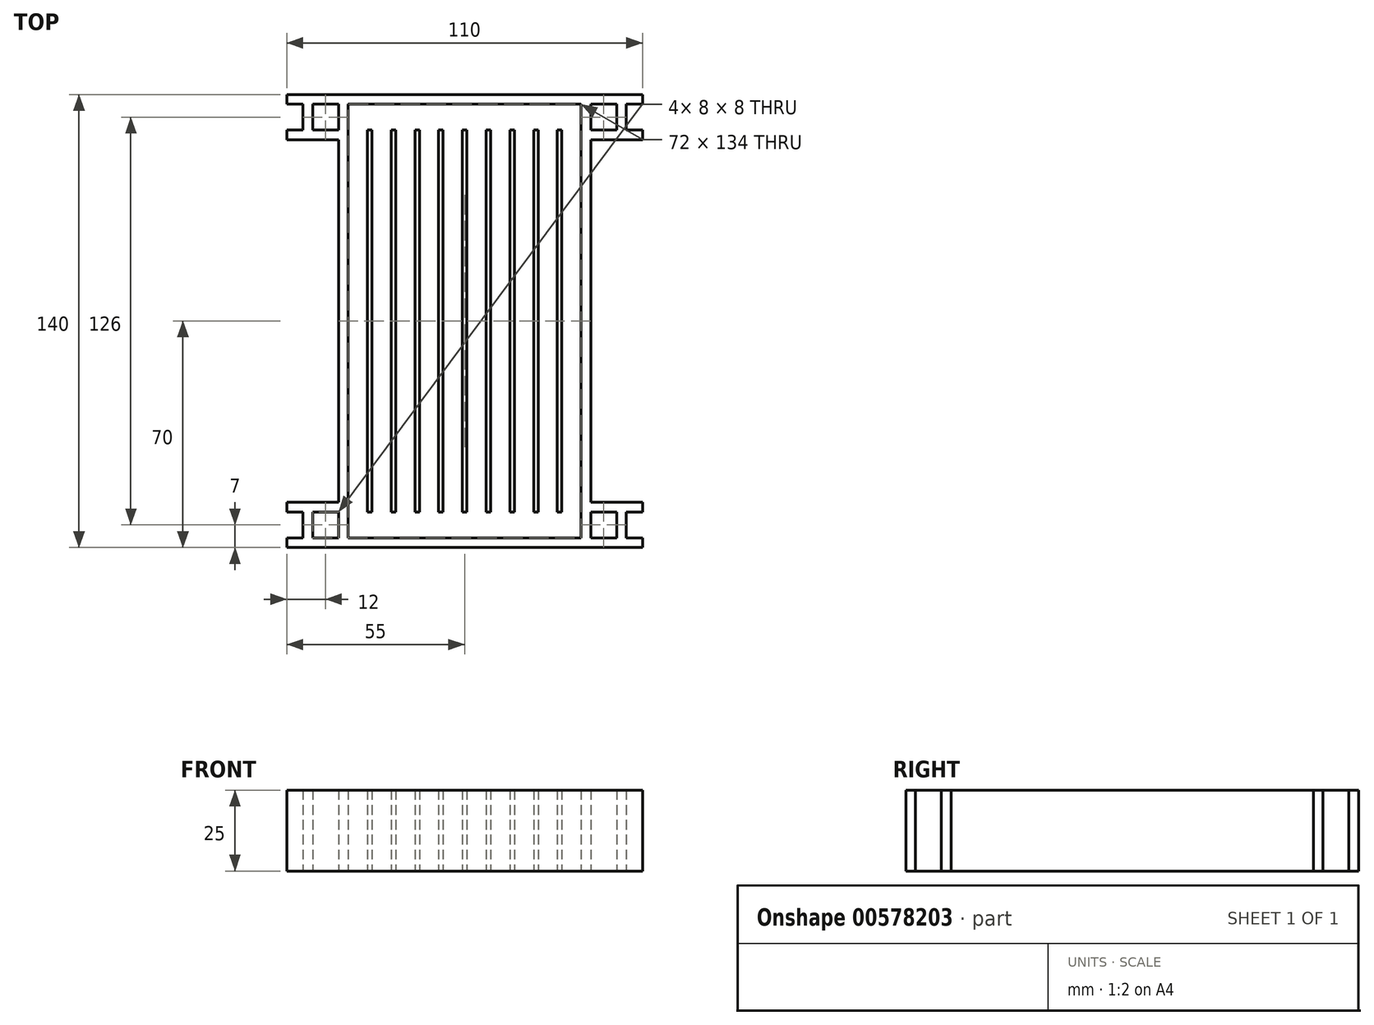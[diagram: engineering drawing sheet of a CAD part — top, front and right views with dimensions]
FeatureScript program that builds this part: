
annotation { "Feature Type Name" : "Feature", "Feature Type Description" : "" }
export const myFeature = defineFeature(function(context is Context, id is Id, definition is map)
    precondition{}
    {
        {
            var Q0;
            Q0=qCreatedBy(makeId("Top.planeOp"),FACE);
            var sketch = newSketch(context, id + "F0", { "sketchPlane" : qUnion([Q0])});
            skLineSegment(sketch, "E0.bottom", {"start": v(-55, 70) * mm, "end": v(55, 70) * mm});
            skLineSegment(sketch, "E0.top", {"start": v(-55, -70) * mm, "end": v(55, -70) * mm});
            skLineSegment(sketch, "E0.left", {"start": v(-55, 70) * mm, "end": v(-55, 67) * mm});
            skLineSegment(sketch, "E0.right", {"start": v(55, 70) * mm, "end": v(55, 67) * mm});
            skLineSegment(sketch, "E1", {"start": v(-55, 67) * mm, "end": v(-50, 67) * mm});
            skLineSegment(sketch, "E2", {"start": v(-50, 67) * mm, "end": v(-50, 59) * mm});
            skLineSegment(sketch, "E3", {"start": v(-39, 67) * mm, "end": v(-39, 59) * mm});
            skLineSegment(sketch, "E4", {"start": v(-50, 56) * mm, "end": v(-39, 56) * mm});
            skLineSegment(sketch, "E5", {"start": v(-47, 67) * mm, "end": v(-47, 59) * mm});
            skLineSegment(sketch, "E6", {"start": v(-47, 59) * mm, "end": v(-39, 59) * mm});
            skLineSegment(sketch, "E7", {"start": v(-36, 67) * mm, "end": v(-36, 0) * mm});
            skLineSegment(sketch, "E8.bottom", {"start": v(-30.06, 59) * mm, "end": v(-28.66, 59) * mm});
            skLineSegment(sketch, "E8.left", {"start": v(-30.06, 59) * mm, "end": v(-30.06, 0) * mm});
            skLineSegment(sketch, "E8.right", {"start": v(-28.66, 59) * mm, "end": v(-28.66, 0) * mm});
            skLineSegment(sketch, "E9.MirrorCS", {"start": v(39, 67) * mm, "end": v(39, 59) * mm});
            skLineSegment(sketch, "E10.MirrorCS", {"start": v(36, 67) * mm, "end": v(36, 0) * mm});
            skLineSegment(sketch, "E11.MirrorCS", {"start": v(47, 59) * mm, "end": v(39, 59) * mm});
            skLineSegment(sketch, "E12.MirrorCS", {"start": v(50, 56) * mm, "end": v(39, 56) * mm});
            skLineSegment(sketch, "E13.MirrorCS", {"start": v(50, 67) * mm, "end": v(50, 59) * mm});
            skLineSegment(sketch, "E14.MirrorCS", {"start": v(47, 67) * mm, "end": v(47, 59) * mm});
            skLineSegment(sketch, "E15.1.0.0", {"start": v(-21.32, 59) * mm, "end": v(-21.32, 0) * mm});
            skLineSegment(sketch, "E15.1.0.1", {"start": v(-22.72, 59) * mm, "end": v(-22.72, 0) * mm});
            skLineSegment(sketch, "E15.1.0.2", {"start": v(-22.72, 59) * mm, "end": v(-21.32, 59) * mm});
            skLineSegment(sketch, "E15.2.0.0", {"start": v(-13.98, 59) * mm, "end": v(-13.98, 0) * mm});
            skLineSegment(sketch, "E15.2.0.1", {"start": v(-15.38, 59) * mm, "end": v(-15.38, 0) * mm});
            skLineSegment(sketch, "E15.2.0.2", {"start": v(-15.38, 59) * mm, "end": v(-13.98, 59) * mm});
            skLineSegment(sketch, "E15.3.0.0", {"start": v(-6.64, 59) * mm, "end": v(-6.64, 0) * mm});
            skLineSegment(sketch, "E15.3.0.1", {"start": v(-8.04, 59) * mm, "end": v(-8.04, 0) * mm});
            skLineSegment(sketch, "E15.3.0.2", {"start": v(-8.04, 59) * mm, "end": v(-6.64, 59) * mm});
            skLineSegment(sketch, "E15.4.0.0", {"start": v(0.7, 59) * mm, "end": v(0.7, 0) * mm});
            skLineSegment(sketch, "E15.4.0.1", {"start": v(-0.7, 59) * mm, "end": v(-0.7, 0) * mm});
            skLineSegment(sketch, "E15.4.0.2", {"start": v(-0.7, 59) * mm, "end": v(0.7, 59) * mm});
            skLineSegment(sketch, "E15.5.0.0", {"start": v(8.04, 59) * mm, "end": v(8.04, 0) * mm});
            skLineSegment(sketch, "E15.5.0.1", {"start": v(6.64, 59) * mm, "end": v(6.64, 0) * mm});
            skLineSegment(sketch, "E15.5.0.2", {"start": v(6.64, 59) * mm, "end": v(8.04, 59) * mm});
            skLineSegment(sketch, "E15.6.0.0", {"start": v(15.38, 59) * mm, "end": v(15.38, 0) * mm});
            skLineSegment(sketch, "E15.6.0.1", {"start": v(13.98, 59) * mm, "end": v(13.98, 0) * mm});
            skLineSegment(sketch, "E15.6.0.2", {"start": v(13.98, 59) * mm, "end": v(15.38, 59) * mm});
            skLineSegment(sketch, "E15.7.0.0", {"start": v(22.72, 59) * mm, "end": v(22.72, 0) * mm});
            skLineSegment(sketch, "E15.7.0.1", {"start": v(21.32, 59) * mm, "end": v(21.32, 0) * mm});
            skLineSegment(sketch, "E15.7.0.2", {"start": v(21.32, 59) * mm, "end": v(22.72, 59) * mm});
            skLineSegment(sketch, "E15.8.0.0", {"start": v(30.06, 59) * mm, "end": v(30.06, 0) * mm});
            skLineSegment(sketch, "E15.8.0.1", {"start": v(28.66, 59) * mm, "end": v(28.66, 0) * mm});
            skLineSegment(sketch, "E15.8.0.2", {"start": v(28.66, 59) * mm, "end": v(30.06, 59) * mm});
            skLineSegment(sketch, "E16", {"start": v(-50, 59) * mm, "end": v(-55, 59) * mm});
            skLineSegment(sketch, "E17.MirrorCS", {"start": v(50, 59) * mm, "end": v(55, 59) * mm});
            skLineSegment(sketch, "E18", {"start": v(-50, 56) * mm, "end": v(-55, 56) * mm});
            skLineSegment(sketch, "E19.MirrorCS", {"start": v(50, 56) * mm, "end": v(55, 56) * mm});
            skLineSegment(sketch, "E20.MirrorCS", {"start": v(28.66, -59) * mm, "end": v(30.06, -59) * mm});
            skLineSegment(sketch, "E21.MirrorCS", {"start": v(-0.7, -59) * mm, "end": v(0.7, -59) * mm});
            skLineSegment(sketch, "E22.MirrorCS", {"start": v(-30.06, -59) * mm, "end": v(-28.66, -59) * mm});
            skLineSegment(sketch, "E23.MirrorCS", {"start": v(13.98, -59) * mm, "end": v(15.38, -59) * mm});
            skLineSegment(sketch, "E24.MirrorCS", {"start": v(-15.38, -59) * mm, "end": v(-13.98, -59) * mm});
            skLineSegment(sketch, "E25.MirrorCS", {"start": v(6.64, -59) * mm, "end": v(8.04, -59) * mm});
            skLineSegment(sketch, "E26.MirrorCS", {"start": v(-22.72, -59) * mm, "end": v(-21.32, -59) * mm});
            skLineSegment(sketch, "E27.MirrorCS", {"start": v(21.32, -59) * mm, "end": v(22.72, -59) * mm});
            skLineSegment(sketch, "E28.MirrorCS", {"start": v(-8.04, -59) * mm, "end": v(-6.64, -59) * mm});
            skLineSegment(sketch, "E29.MirrorCS", {"start": v(-0.7, -59) * mm, "end": v(-0.7, 0) * mm});
            skLineSegment(sketch, "E30.MirrorCS", {"start": v(28.66, -59) * mm, "end": v(28.66, 0) * mm});
            skLineSegment(sketch, "E31.MirrorCS", {"start": v(50, -56) * mm, "end": v(39, -56) * mm});
            skLineSegment(sketch, "E32.MirrorCS", {"start": v(-13.98, -59) * mm, "end": v(-13.98, 0) * mm});
            skLineSegment(sketch, "E33.MirrorCS", {"start": v(15.38, -59) * mm, "end": v(15.38, 0) * mm});
            skLineSegment(sketch, "E34.MirrorCS", {"start": v(50, -56) * mm, "end": v(55, -56) * mm});
            skLineSegment(sketch, "E35.MirrorCS", {"start": v(13.98, -59) * mm, "end": v(13.98, 0) * mm});
            skLineSegment(sketch, "E36.MirrorCS", {"start": v(-15.38, -59) * mm, "end": v(-15.38, 0) * mm});
            skLineSegment(sketch, "E37.MirrorCS", {"start": v(-50, -67) * mm, "end": v(-50, -59) * mm});
            skLineSegment(sketch, "E38.MirrorCS", {"start": v(50, -67) * mm, "end": v(50, -59) * mm});
            skLineSegment(sketch, "E39.MirrorCS", {"start": v(-39, -67) * mm, "end": v(-39, -59) * mm});
            skLineSegment(sketch, "E40.MirrorCS", {"start": v(-50, -56) * mm, "end": v(-39, -56) * mm});
            skLineSegment(sketch, "E41.MirrorCS", {"start": v(-47, -67) * mm, "end": v(-47, -59) * mm});
            skLineSegment(sketch, "E42.MirrorCS", {"start": v(-47, -59) * mm, "end": v(-39, -59) * mm});
            skLineSegment(sketch, "E43.MirrorCS", {"start": v(-36, -67) * mm, "end": v(-36, 0) * mm});
            skLineSegment(sketch, "E44.MirrorCS", {"start": v(47, -67) * mm, "end": v(47, -59) * mm});
            skLineSegment(sketch, "E45.MirrorCS", {"start": v(50, -59) * mm, "end": v(55, -59) * mm});
            skLineSegment(sketch, "E46.MirrorCS", {"start": v(36, -67) * mm, "end": v(36, 0) * mm});
            skLineSegment(sketch, "E47.MirrorCS", {"start": v(22.72, -59) * mm, "end": v(22.72, 0) * mm});
            skLineSegment(sketch, "E48.MirrorCS", {"start": v(-6.64, -59) * mm, "end": v(-6.64, 0) * mm});
            skLineSegment(sketch, "E49.MirrorCS", {"start": v(30.06, -59) * mm, "end": v(30.06, 0) * mm});
            skLineSegment(sketch, "E50.MirrorCS", {"start": v(47, -59) * mm, "end": v(39, -59) * mm});
            skLineSegment(sketch, "E51.MirrorCS", {"start": v(-50, -56) * mm, "end": v(-55, -56) * mm});
            skLineSegment(sketch, "E52.MirrorCS", {"start": v(39, -67) * mm, "end": v(39, -59) * mm});
            skLineSegment(sketch, "E53.MirrorCS", {"start": v(-28.66, -59) * mm, "end": v(-28.66, 0) * mm});
            skLineSegment(sketch, "E54.MirrorCS", {"start": v(-22.72, -59) * mm, "end": v(-22.72, 0) * mm});
            skLineSegment(sketch, "E55.MirrorCS", {"start": v(-21.32, -59) * mm, "end": v(-21.32, 0) * mm});
            skLineSegment(sketch, "E56.MirrorCS", {"start": v(-55, -67) * mm, "end": v(-50, -67) * mm});
            skLineSegment(sketch, "E57.MirrorCS", {"start": v(0.7, -59) * mm, "end": v(0.7, 0) * mm});
            skLineSegment(sketch, "E58.MirrorCS", {"start": v(21.32, -59) * mm, "end": v(21.32, 0) * mm});
            skLineSegment(sketch, "E59.MirrorCS", {"start": v(-30.06, -59) * mm, "end": v(-30.06, 0) * mm});
            skLineSegment(sketch, "E60.MirrorCS", {"start": v(-8.04, -59) * mm, "end": v(-8.04, 0) * mm});
            skLineSegment(sketch, "E61.MirrorCS", {"start": v(-50, -59) * mm, "end": v(-55, -59) * mm});
            skLineSegment(sketch, "E62.MirrorCS", {"start": v(6.64, -59) * mm, "end": v(6.64, 0) * mm});
            skLineSegment(sketch, "E63.MirrorCS", {"start": v(8.04, -59) * mm, "end": v(8.04, 0) * mm});
            skPoint(sketch, "E64", {"position": v(0, 0) * mm});
            skPoint(sketch, "E65.orphan", {"position": v(50, -56) * mm});
            skLineSegment(sketch, "E66.trimOffspring", {"start": v(39, -56) * mm, "end": v(39, 0) * mm});
            skLineSegment(sketch, "E67.trimOffspring", {"start": v(-39, -56) * mm, "end": v(-39, 0) * mm});
            skLineSegment(sketch, "E68.trimOffspring", {"start": v(-47, -67) * mm, "end": v(-39, -67) * mm});
            skLineSegment(sketch, "E69.trimOffspring", {"start": v(-36, -67) * mm, "end": v(36, -67) * mm});
            skLineSegment(sketch, "E70.trimOffspring", {"start": v(39, -67) * mm, "end": v(47, -67) * mm});
            skLineSegment(sketch, "E71.trimOffspring", {"start": v(50, -67) * mm, "end": v(55, -67) * mm});
            skLineSegment(sketch, "E72.trimOffspring", {"start": v(-55, -67) * mm, "end": v(-55, -70) * mm});
            skLineSegment(sketch, "E73.trimOffspring", {"start": v(-47, 67) * mm, "end": v(-39, 67) * mm});
            skLineSegment(sketch, "E74.trimOffspring", {"start": v(-36, 67) * mm, "end": v(36, 67) * mm});
            skLineSegment(sketch, "E75.trimOffspring", {"start": v(39, 67) * mm, "end": v(47, 67) * mm});
            skLineSegment(sketch, "E76.trimOffspring", {"start": v(50, 67) * mm, "end": v(55, 67) * mm});
            skLineSegment(sketch, "E77.trimOffspring", {"start": v(39, 56) * mm, "end": v(39, 0) * mm});
            skPoint(sketch, "E78.orphan", {"position": v(50, 56) * mm});
            skLineSegment(sketch, "E79.trimOffspring", {"start": v(55, 59) * mm, "end": v(55, 56) * mm});
            skLineSegment(sketch, "E80.trimOffspring", {"start": v(55, -67) * mm, "end": v(55, -70) * mm});
            skLineSegment(sketch, "E81.trimOffspring", {"start": v(-55, 59) * mm, "end": v(-55, 56) * mm});
            skLineSegment(sketch, "E82.trimOffspring", {"start": v(-55, -56) * mm, "end": v(-55, -59) * mm});
            skLineSegment(sketch, "E83.trimOffspring", {"start": v(55, -56) * mm, "end": v(55, -59) * mm});
            skLineSegment(sketch, "E84.trimOffspring", {"start": v(-39, 56) * mm, "end": v(-39, 0) * mm});
            skSolve(sketch);
        }
        {
            var Q0;
            Q0=makeQuery(id+"F0.imprint","IMPRINT",FACE,{"disambiguationData":[TD([[makeQuery(id+"F0.imprint","IMPRINT",EDGE,{"derivedFrom":sQuery(id+"F0.wireOp",EDGE,"E15.7.0.0")}),-1.0]])]});
            var Q1;
            Q1=makeQuery(id+"F0.imprint","IMPRINT",FACE,{"disambiguationData":[TD([[makeQuery(id+"F0.imprint","IMPRINT",EDGE,{"derivedFrom":sQuery(id+"F0.wireOp",EDGE,"E15.5.0.0")}),-1.0]])]});
            var Q2;
            Q2=makeQuery(id+"F0.imprint","IMPRINT",FACE,{"disambiguationData":[TD([[makeQuery(id+"F0.imprint","IMPRINT",EDGE,{"derivedFrom":sQuery(id+"F0.wireOp",EDGE,"E15.4.0.0")}),-1.0]])]});
            var Q3;
            Q3=makeQuery(id+"F0.imprint","IMPRINT",FACE,{"disambiguationData":[TD([[makeQuery(id+"F0.imprint","IMPRINT",EDGE,{"derivedFrom":sQuery(id+"F0.wireOp",EDGE,"E15.2.0.0")}),-1.0]])]});
            var Q4;
            Q4=makeQuery(id+"F0.imprint","IMPRINT",FACE,{"disambiguationData":[TD([[makeQuery(id+"F0.imprint","IMPRINT",EDGE,{"derivedFrom":sQuery(id+"F0.wireOp",EDGE,"E15.1.0.0")}),-1.0]])]});
            var Q5;
            Q5=makeQuery(id+"F0.imprint","IMPRINT",FACE,{"disambiguationData":[TD([[makeQuery(id+"F0.imprint","IMPRINT",EDGE,{"derivedFrom":sQuery(id+"F0.wireOp",EDGE,"E0.bottom")}),-1.0]])]});
            var Q6;
            Q6=makeQuery(id+"F0.imprint","IMPRINT",FACE,{"disambiguationData":[TD([[makeQuery(id+"F0.imprint","IMPRINT",EDGE,{"derivedFrom":sQuery(id+"F0.wireOp",EDGE,"E8.bottom")}),-1.0]])]});
            var Q7;
            Q7=makeQuery(id+"F0.imprint","IMPRINT",FACE,{"disambiguationData":[TD([[makeQuery(id+"F0.imprint","IMPRINT",EDGE,{"derivedFrom":sQuery(id+"F0.wireOp",EDGE,"E15.8.0.0")}),-1.0]])]});
            var Q8;
            Q8=makeQuery(id+"F0.imprint","IMPRINT",FACE,{"disambiguationData":[TD([[makeQuery(id+"F0.imprint","IMPRINT",EDGE,{"derivedFrom":sQuery(id+"F0.wireOp",EDGE,"E15.6.0.0")}),-1.0]])]});
            var Q9;
            Q9=makeQuery(id+"F0.imprint","IMPRINT",FACE,{"disambiguationData":[TD([[makeQuery(id+"F0.imprint","IMPRINT",EDGE,{"derivedFrom":sQuery(id+"F0.wireOp",EDGE,"E15.3.0.0")}),-1.0]])]});
            extrude(context, id + "F1", {"entities" : qUnion([Q0, Q1, Q2, Q3, Q4, Q5, Q6, Q7, Q8, Q9]), "depth" : 25 * mm, "offsetDistance" : 25 * mm});
        }
    });
